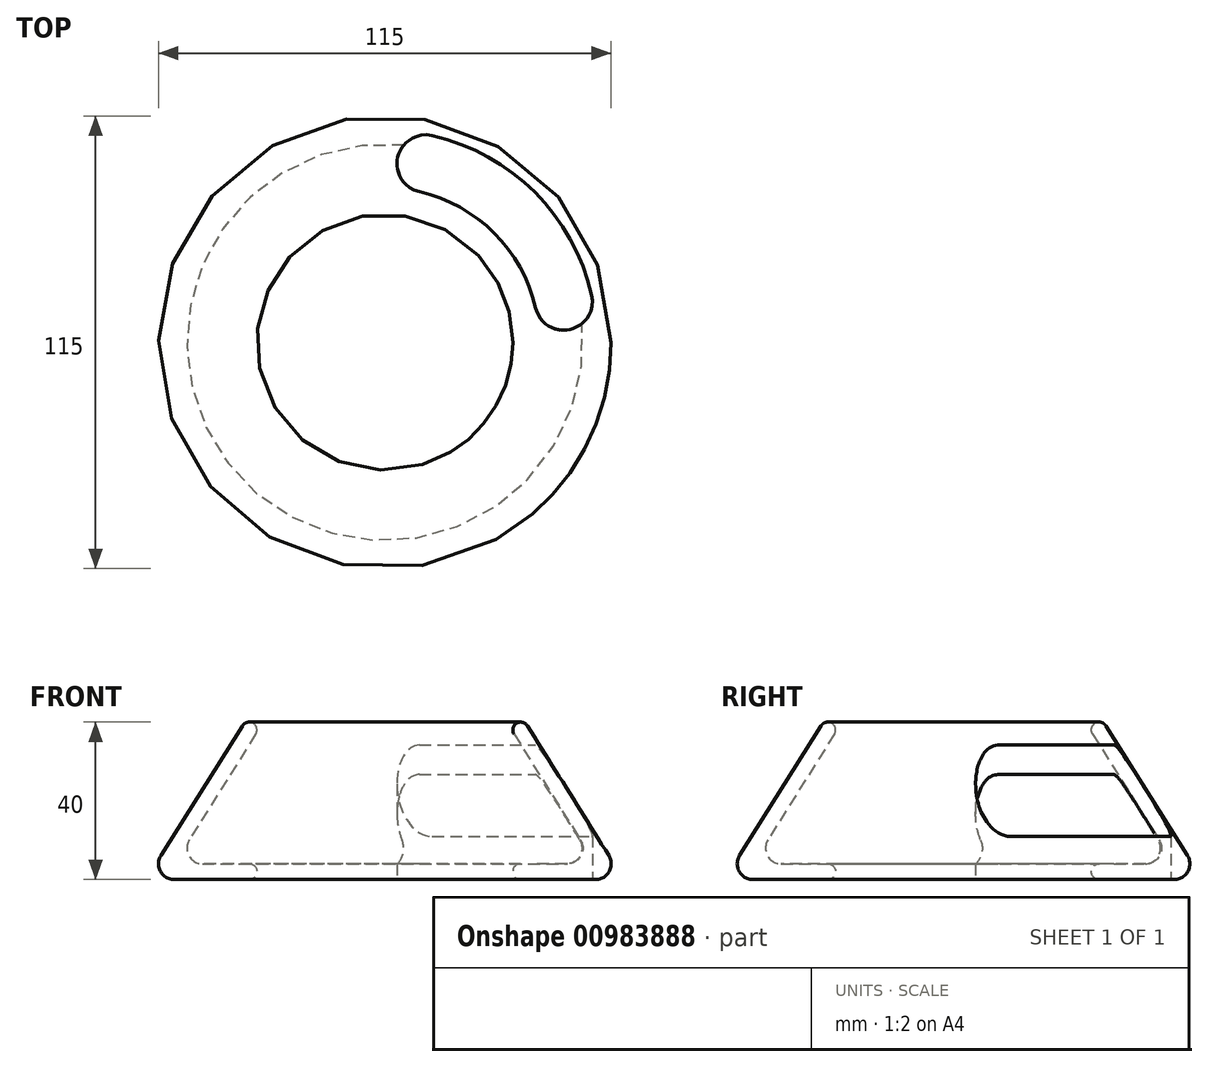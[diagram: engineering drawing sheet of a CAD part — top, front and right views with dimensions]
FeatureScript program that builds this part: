
annotation { "Feature Type Name" : "Feature", "Feature Type Description" : "" }
export const myFeature = defineFeature(function(context is Context, id is Id, definition is map)
    precondition{}
    {
        {
            var Q0;
            Q0=qCreatedBy(makeId("Front.planeOp"),FACE);
            var sketch = newSketch(context, id + "F0", { "sketchPlane" : qUnion([Q0])});
            skLineSegment(sketch, "E0", {"start": v(32.8, 36.94) * mm, "end": v(49.7, 10.06) * mm});
            skLineSegment(sketch, "E1", {"start": v(46.34, 4) * mm, "end": v(34.5, 4) * mm});
            skLineSegment(sketch, "E2", {"start": v(36.2, 39.06) * mm, "end": v(56.89, 6.13) * mm});
            skLineSegment(sketch, "E3", {"start": v(53.5, 0) * mm, "end": v(34.5, 0) * mm});
            skLineSegment(sketch, "E4", {"start": v(0, 188.72) * mm, "end": v(0, 0) * mm, "construction": true});
            skArc(sketch, "E5", {"start": v(36.2, 39.06) * mm, "mid": v(33.44, 39.7) * mm, "end": v(32.8, 36.94) * mm});
            skArc(sketch, "E6", {"start": v(53.5, 0) * mm, "mid": v(57, 2.07) * mm, "end": v(56.89, 6.13) * mm});
            skArc(sketch, "E7", {"start": v(46.34, 4) * mm, "mid": v(49.8, 6.04) * mm, "end": v(49.7, 10.06) * mm});
            skArc(sketch, "E8", {"start": v(34.5, 4) * mm, "mid": v(32.5, 2) * mm, "end": v(34.5, 0) * mm});
            skSolve(sketch);
        }
        {
            var Q0;
            Q0=makeQuery(id+"F0.imprint","IMPRINT",FACE,{"disambiguationData":[TD([[makeQuery(id+"F0.imprint","IMPRINT",EDGE,{"derivedFrom":sQuery(id+"F0.wireOp",EDGE,"E0")}),1.0]])]});
            var Q1;
            Q1=sQuery(id+"F0.wireOp",EDGE,"E4");
            revolve(context, id + "F1", {"surfaceOperationType" : NewSurfaceOperationType.NEW, "entities" : qUnion([Q0]), "axis" : qUnion([Q1]), "revolveType" : RevolveType.FULL});
        }
        {
            var Q0;
            Q0=qCreatedBy(makeId("Top.planeOp"),FACE);
            var sketch = newSketch(context, id + "F2", { "sketchPlane" : qUnion([Q0])});
            skLineSegment(sketch, "E9", {"start": v(0, 0) * mm, "end": v(59.34, 59.34) * mm, "construction": true});
            skArc(sketch, "E10", {"start": v(38.26, 8.76) * mm, "mid": v(34.35, 19) * mm, "end": v(27.76, 27.76) * mm});
            skArc(sketch, "E11", {"start": v(52.53, 12.03) * mm, "mid": v(47.15, 26.08) * mm, "end": v(38.1, 38.1) * mm});
            skArc(sketch, "E12", {"start": v(38.26, 8.76) * mm, "mid": v(47.03, 3.26) * mm, "end": v(52.53, 12.03) * mm});
            skArc(sketch, "E13.MirrorCS", {"start": v(12.03, 52.53) * mm, "mid": v(26.08, 47.15) * mm, "end": v(38.1, 38.1) * mm});
            skArc(sketch, "E14.MirrorCS", {"start": v(8.76, 38.26) * mm, "mid": v(3.26, 47.03) * mm, "end": v(12.03, 52.53) * mm});
            skArc(sketch, "E15.MirrorCS", {"start": v(8.76, 38.26) * mm, "mid": v(19, 34.35) * mm, "end": v(27.76, 27.76) * mm});
            skSolve(sketch);
        }
        {
            var Q0;
            Q0 = qSketchRegion(id + "F2", true);
            extrude(context, id + "F3", {"entities" : qUnion([Q0]), "operationType" : NewBodyOperationType.REMOVE, "endBound" : BoundingType.THROUGH_ALL, "depth" : 25 * mm, "offsetDistance" : 25 * mm});
        }
    });
